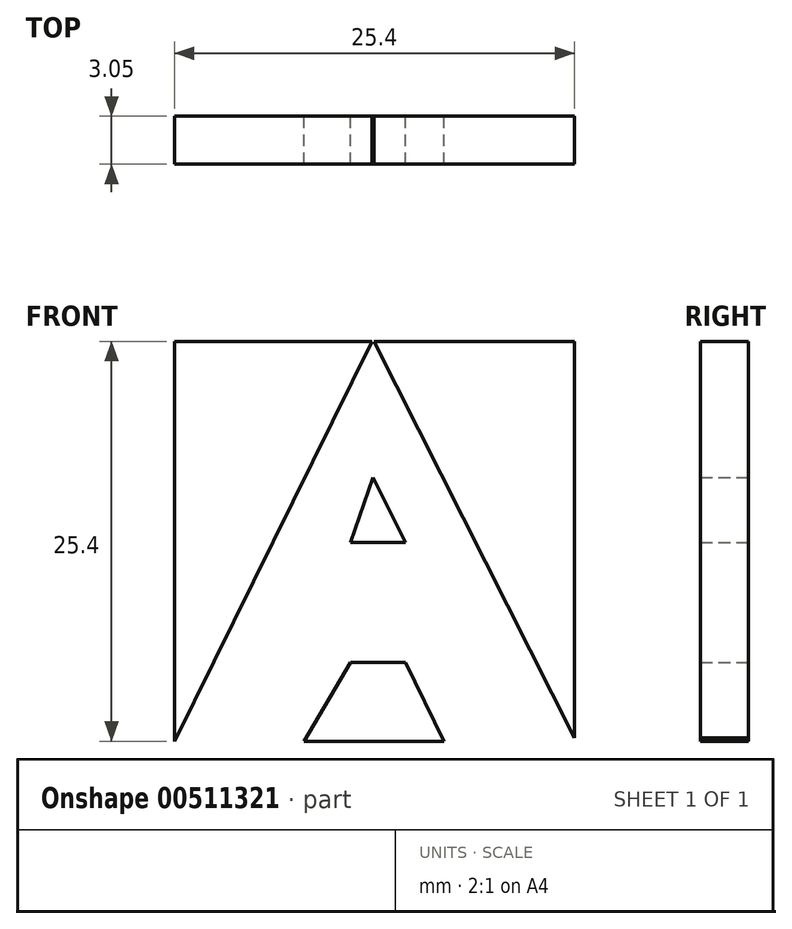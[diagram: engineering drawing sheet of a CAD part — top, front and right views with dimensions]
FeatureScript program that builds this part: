
annotation { "Feature Type Name" : "Feature", "Feature Type Description" : "" }
export const myFeature = defineFeature(function(context is Context, id is Id, definition is map)
    precondition{}
    {
        {
            var Q0;
            Q0=qCreatedBy(makeId("Front.planeOp"),FACE);
            var sketch = newSketch(context, id + "F0", { "sketchPlane" : qUnion([Q0])});
            skLineSegment(sketch, "E0", {"start": v(0, 0) * mm, "end": v(0, 25.4) * mm});
            skLineSegment(sketch, "E1", {"start": v(0, 25.4) * mm, "end": v(25.4, 25.4) * mm});
            skLineSegment(sketch, "E2", {"start": v(25.4, 25.4) * mm, "end": v(25.4, 0) * mm});
            skLineSegment(sketch, "E3", {"start": v(25.4, 0) * mm, "end": v(0, 0) * mm});
            skLineSegment(sketch, "E4", {"start": v(12.7, 25.4) * mm, "end": v(0, 0) * mm});
            skLineSegment(sketch, "E5", {"start": v(12.7, 25.4) * mm, "end": v(25.4, 0) * mm});
            skLineSegment(sketch, "E6", {"start": v(12.7, 12.7) * mm, "end": v(12.7, 12.7) * mm});
            skLineSegment(sketch, "E7", {"start": v(17.02, 0) * mm, "end": v(14.45, 5.14) * mm});
            skLineSegment(sketch, "E8", {"start": v(14.45, 5.14) * mm, "end": v(10.95, 5.14) * mm});
            skLineSegment(sketch, "E9", {"start": v(10.95, 5.14) * mm, "end": v(8.38, 0) * mm});
            skPoint(sketch, "E10.orphan", {"position": v(6.35, 12.7) * mm});
            skPoint(sketch, "E11.orphan", {"position": v(19.05, 12.7) * mm});
            skLineSegment(sketch, "E12", {"start": v(10.6, 12.7) * mm, "end": v(14.8, 12.7) * mm});
            skLineSegment(sketch, "E13", {"start": v(10.6, 12.7) * mm, "end": v(12.7, 16.92) * mm});
            skLineSegment(sketch, "E14", {"start": v(12.7, 16.92) * mm, "end": v(14.8, 12.7) * mm});
            skSolve(sketch);
        }
        {
            var Q0;
            Q0 = qSketchRegion(id + "F0", true);
            var Q1;
            Q1=makeQuery(id+"F0.imprint","IMPRINT",FACE,{"disambiguationData":[TD([[makeQuery(id+"F0.imprint","IMPRINT",EDGE,{"derivedFrom":sQuery(id+"F0.wireOp",EDGE,"E12")}),1.0]])]});
            extrude(context, id + "F1", {"entities" : qUnion([Q0, Q1]), "depth" : 3.05 * mm, "offsetDistance" : 25.4 * mm});
        }
        {
            var Q0;
            Q0=qCreatedBy(makeId("Front.planeOp"),FACE);
            var sketch = newSketch(context, id + "F2", { "sketchPlane" : qUnion([Q0])});
            skLineSegment(sketch, "E15", {"start": v(0, 0) * mm, "end": v(12.6, 25.53) * mm});
            skLineSegment(sketch, "E16", {"start": v(12.6, 25.53) * mm, "end": v(25.51, 0) * mm});
            skLineSegment(sketch, "E17", {"start": v(25.51, 0) * mm, "end": v(17.12, 0) * mm});
            skLineSegment(sketch, "E18", {"start": v(17.12, 0) * mm, "end": v(14.67, 5) * mm});
            skLineSegment(sketch, "E19", {"start": v(14.67, 5) * mm, "end": v(11.18, 5) * mm});
            skLineSegment(sketch, "E20", {"start": v(11.18, 5) * mm, "end": v(8.2, 0) * mm});
            skLineSegment(sketch, "E21", {"start": v(8.2, 0) * mm, "end": v(0, 0) * mm});
            skLineSegment(sketch, "E22", {"start": v(11.18, 12.62) * mm, "end": v(14.67, 12.62) * mm});
            skLineSegment(sketch, "E23", {"start": v(12.6, 16.75) * mm, "end": v(11.18, 12.62) * mm});
            skLineSegment(sketch, "E24", {"start": v(14.67, 12.62) * mm, "end": v(12.6, 16.75) * mm});
            skLineSegment(sketch, "E25", {"start": v(14.67, 12.62) * mm, "end": v(11.18, 12.62) * mm});
            skSolve(sketch);
        }
        {
            var Q0;
            Q0 = qSketchRegion(id + "F2", true);
            extrude(context, id + "F3", {"entities" : qUnion([Q0]), "operationType" : NewBodyOperationType.REMOVE, "depth" : 25.4 * mm, "offsetDistance" : 25.4 * mm});
        }
    });
